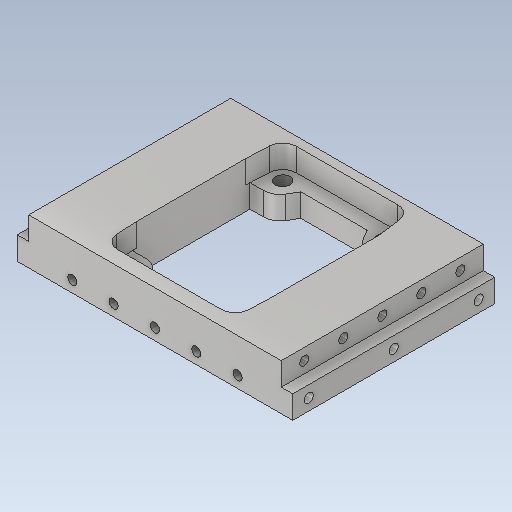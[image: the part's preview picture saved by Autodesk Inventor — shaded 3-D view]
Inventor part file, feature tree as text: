
AUTODESK INVENTOR PART (.ipt)
format: ipt  version: 2020 (Build 240168000, 168)  size: 450,048 bytes
history: native  units: mm
features: sketch x14, extrude x7, thread x7, reference x6, hole x5, other x4, projected_geometry x4, pattern_linear x3, thicken_offset x2, plane x1, mirror x1
ambient origin geometry x8: Origin, YZ Plane, XZ Plane, XY Plane, X Axis, Y Axis, Z Axis, Center Point
bodies: Body1 (feature_tree)
feature tree (54):
  other  "Твердое тело1"
  extrude  "Выдавливание1"  Depth=10.0mm TaperAngle=0.0deg
  extrude  "Extrusion2"  Depth=10.0mm TaperAngle=0.0deg
  extrude  "Extrusion3"  Depth=10.0mm TaperAngle=0.0deg
  extrude  "Extrusion4"  Depth=88.0mm
  sketch  "Sketch Driven Pattern1"  dims[d0=90.0deg d1=10.0mm d2=0.0mm]
  thread  "Thread5"  [1 undecoded]
  thread  "Thread6"  [1 undecoded]
  thread  "Thread7"  [1 undecoded]
  thread  "Thread8"  [1 undecoded]
  extrude  "Extrusion7"  Depth=10.0mm TaperAngle=0.0deg
  extrude  "Extrusion8"  Depth=0.772096mm
  extrude  "Extrusion9"  Depth=58.0mm
  hole  "Hole7"  [1 undecoded]
  thread  "Thread13"  [1 undecoded]
  pattern_linear  "Rectangular Pattern7"  Spacing1=10.0mm  [1 undecoded]
  hole  "Hole8"  [1 undecoded]
  thread  "Thread14"  [1 undecoded]
  pattern_linear  "Rectangular Pattern8"  Spacing1=10.0mm  [1 undecoded]
  hole  "Hole9"  [1 undecoded]
  thread  "Thread15"  [1 undecoded]
  pattern_linear  "Rectangular Pattern9"  Spacing1=5.0mm  [1 undecoded]
  plane  "Work Plane2"
  mirror  "Mirror6"
  hole  "Hole10"  [1 undecoded]
  hole  "Hole11"  [1 undecoded]
  thicken_offset  "Thicken1"
  thicken_offset  "Thicken2"
  sketch  "Эскиз1"
  sketch  "Sketch3"  dims[d7=10.0mm d8=0.0mm d9=10.0mm d10=0.0mm]
  sketch  "Sketch4"  dims[d11=12.0mm d12=10.0mm d13=0.0mm]
  projected_geometry  "Projected Loop2"
  sketch  "Sketch5"  dims[d14=5.0mm d15=88.0mm d16=120.0mm d19=5.0mm d46=10.0mm d47=0.0mm d48=10.0mm d49=0.0mm]
  sketch  "Sketch6"  dims[d50=10.0mm d51=0.0mm d52=10.0mm d53=0.0mm]
  sketch  "Sketch13"  dims[d117=59.544192mm d118=0.772096mm]
  projected_geometry  "Projected Loop3"
  sketch  "Sketch14"  dims[d119=0.772096mm d120=58.0mm]
  projected_geometry  "Projected Loop4"
  sketch  "Sketch15"  dims[d121=10.0mm d122=0.0mm d123=69.407618mm d124=2.203809mm]
  projected_geometry  "Projected Loop5"
  sketch  "Sketch16"  dims[d125=2.203809mm]
  sketch  "Sketch17"  dims[d126=10.0mm d127=0.0mm]
  sketch  "Sketch18"  dims[d128=10.0mm d129=0.0mm]
  sketch  "Sketch19"  dims[d130=10.0mm]
  reference  "Reference5"
  reference  "Reference6"
  reference  "Reference7"
  sketch  "Sketch20"  dims[d131=5.0mm d132=10.0mm d133=4.0mm d134=6.0mm d135=4.0mm d136=2.0mm d137=90.0deg d138=6.0mm d139=120.0deg d140=50.0mm d142=17.0mm d143=10.0mm d144=0.0mm d145=10.0mm d146=5.0mm d147=10.0mm d148=4.0mm d149=6.0mm d150=4.0mm d151=2.0mm d152=90.0deg d153=6.0mm d154=120.0deg d155=10.0mm d156=0.0mm d157=50.0mm d159=17.0mm d160=5.0mm d161=4.0mm d162=6.0mm d163=4.0mm d164=2.0mm d165=90.0deg d166=8.0mm d167=120.0deg d168=10.0mm d169=0.0mm d170=50.0mm d172=18.0mm d173=60.0mm d174=4.0mm d175=6.0mm d176=4.0mm d177=2.0mm d178=90.0deg d179=6.5mm d180=120.0deg d181=4.0mm d182=6.0mm d183=4.0mm d184=2.0mm d185=90.0deg d186=6.5mm d187=120.0deg d188=2.0mm d189=2.0mm d190=2.0mm d191=2.0mm]
  reference  "Reference8"
  reference  "Reference9"
  reference  "Reference10"
  other  "КВ33.000.100 - Блок переключение передач.iam"
  other  "КВ33.000.107 - Крепеж мотора:2"
  other  "КВ33.000.107 - Крепеж мотора:1"
note: 15 required parameter values undecoded (feature->parameter linkage not recoverable at this tier; creation-order binding heuristic only, values carry confidence <= 0.55)
